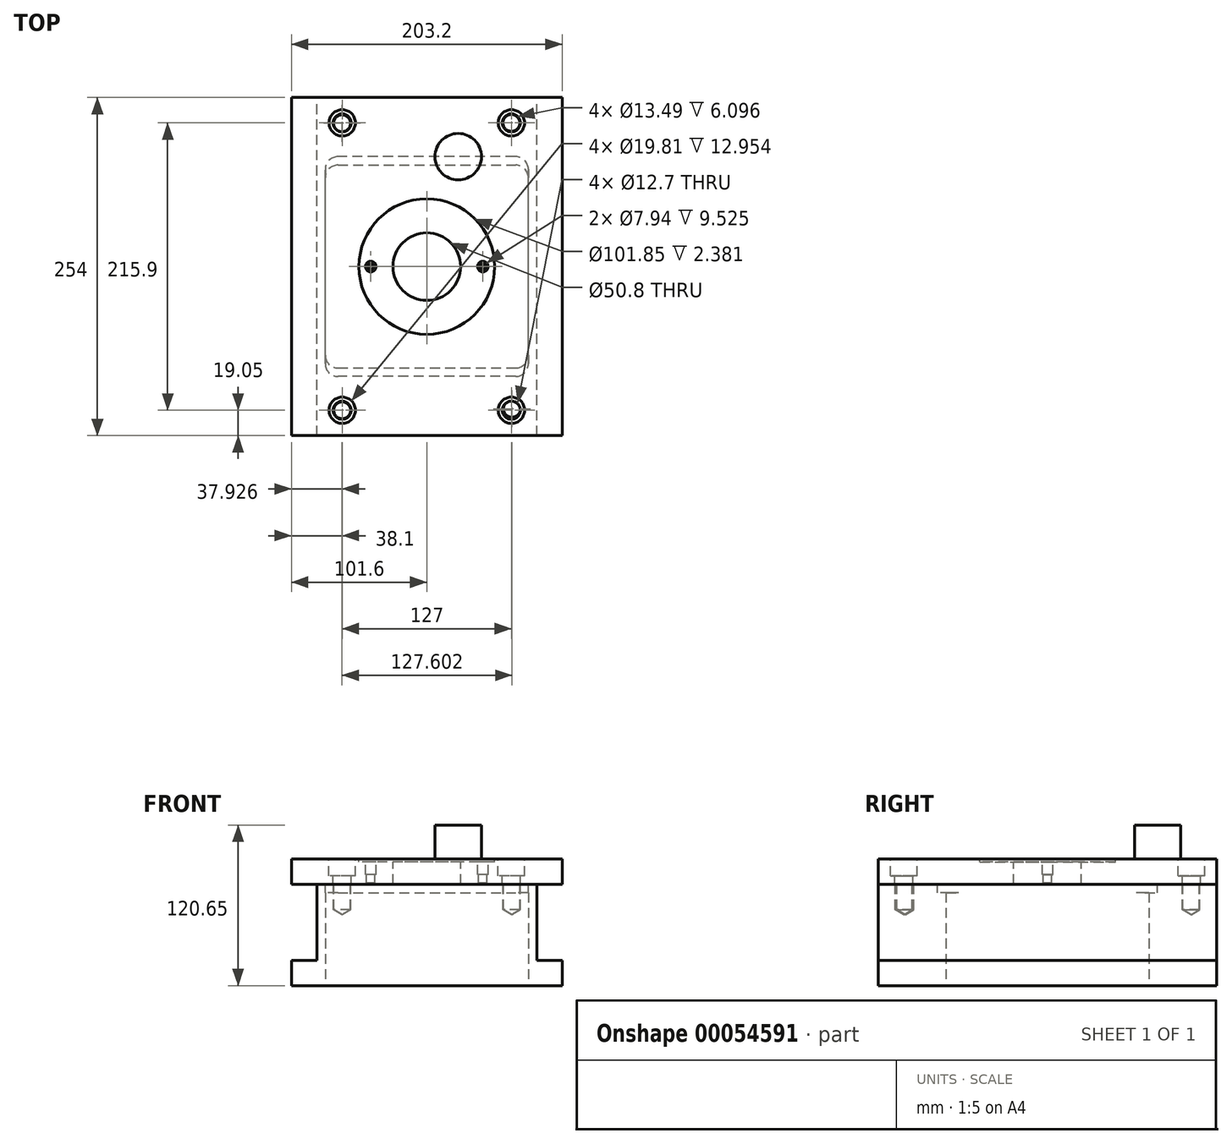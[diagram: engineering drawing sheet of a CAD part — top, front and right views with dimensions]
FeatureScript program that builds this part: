
annotation { "Feature Type Name" : "Feature", "Feature Type Description" : "" }
export const myFeature = defineFeature(function(context is Context, id is Id, definition is map)
    precondition{}
    {
        {
            var Q0;
            Q0=qCreatedBy(makeId("Front.planeOp"),FACE);
            var sketch = newSketch(context, id + "F0", { "sketchPlane" : qUnion([Q0])});
            skLineSegment(sketch, "E0", {"start": v(-101.6, 0) * mm, "end": v(101.6, 0) * mm});
            skLineSegment(sketch, "E1", {"start": v(101.6, 0) * mm, "end": v(101.6, 19.05) * mm});
            skLineSegment(sketch, "E2", {"start": v(101.6, 19.05) * mm, "end": v(82.55, 19.05) * mm});
            skLineSegment(sketch, "E3", {"start": v(82.55, 19.05) * mm, "end": v(82.55, 76.2) * mm});
            skLineSegment(sketch, "E4", {"start": v(82.55, 76.2) * mm, "end": v(-82.55, 76.2) * mm});
            skLineSegment(sketch, "E5", {"start": v(-82.55, 76.2) * mm, "end": v(-82.55, 19.05) * mm});
            skLineSegment(sketch, "E6", {"start": v(-82.55, 19.05) * mm, "end": v(-101.6, 19.05) * mm});
            skLineSegment(sketch, "E7", {"start": v(-101.6, 19.05) * mm, "end": v(-101.6, 0) * mm});
            skSolve(sketch);
        }
        {
            var Q0;
            Q0 = qSketchRegion(id + "F0", true);
            extrude(context, id + "F1", {"entities" : qUnion([Q0]), "endBound" : BoundingType.SYMMETRIC, "depth" : 254 * mm});
        }
        {
            var Q0;
            Q0=makeQuery(id+"F1.opExtrude","SWEPT_FACE",FACE,{"disambiguationData":[OSD([sQuery(id+"F0.wireOp",EDGE,"E0")])]});
            var sketch = newSketch(context, id + "F2", { "sketchPlane" : qUnion([Q0])});
            skLineSegment(sketch, "E8.bottom", {"start": v(-66.67, 76.2) * mm, "end": v(66.67, 76.2) * mm});
            skLineSegment(sketch, "E8.top", {"start": v(-66.67, -76.2) * mm, "end": v(66.67, -76.2) * mm});
            skLineSegment(sketch, "E8.left", {"start": v(-76.2, 66.67) * mm, "end": v(-76.2, -66.68) * mm});
            skLineSegment(sketch, "E8.right", {"start": v(76.2, 66.68) * mm, "end": v(76.2, -66.67) * mm});
            skPoint(sketch, "E9.visualSharp", {"position": v(-76.2, 76.2) * mm});
            skArc(sketch, "E9.filletArc", {"start": v(-66.67, 76.2) * mm, "mid": v(-73.41, 73.41) * mm, "end": v(-76.2, 66.67) * mm});
            skPoint(sketch, "E10.visualSharp", {"position": v(-76.2, -76.2) * mm});
            skArc(sketch, "E10.filletArc", {"start": v(-76.2, -66.68) * mm, "mid": v(-73.41, -73.41) * mm, "end": v(-66.67, -76.2) * mm});
            skPoint(sketch, "E11.visualSharp", {"position": v(76.2, -76.2) * mm});
            skArc(sketch, "E11.filletArc", {"start": v(66.67, -76.2) * mm, "mid": v(73.41, -73.41) * mm, "end": v(76.2, -66.67) * mm});
            skPoint(sketch, "E12.visualSharp", {"position": v(76.2, 76.2) * mm});
            skArc(sketch, "E12.filletArc", {"start": v(76.2, 66.68) * mm, "mid": v(73.41, 73.41) * mm, "end": v(66.67, 76.2) * mm});
            skSolve(sketch);
        }
        {
            var Q0;
            Q0 = qSketchRegion(id + "F2", true);
            extrude(context, id + "F3", {"entities" : qUnion([Q0]), "operationType" : NewBodyOperationType.REMOVE, "oppositeDirection" : true, "depth" : 76.2 * mm});
        }
        {
            var Q0;
            Q0=makeQuery(id+"F1.opExtrude","SWEPT_FACE",FACE,{"disambiguationData":[OSD([sQuery(id+"F0.wireOp",EDGE,"E4")])]});
            var sketch = newSketch(context, id + "F4", { "sketchPlane" : qUnion([Q0])});
            skLineSegment(sketch, "E13.bottom", {"start": v(66.67, 82.55) * mm, "end": v(-66.68, 82.55) * mm});
            skLineSegment(sketch, "E13.top", {"start": v(66.67, -82.55) * mm, "end": v(-66.67, -82.55) * mm});
            skLineSegment(sketch, "E13.left", {"start": v(76.2, 73.03) * mm, "end": v(76.2, -73.03) * mm});
            skLineSegment(sketch, "E13.right", {"start": v(-76.2, 73.03) * mm, "end": v(-76.2, -73.02) * mm});
            skPoint(sketch, "E14.visualSharp", {"position": v(-76.2, 82.55) * mm});
            skArc(sketch, "E14.filletArc", {"start": v(-66.68, 82.55) * mm, "mid": v(-73.41, 79.76) * mm, "end": v(-76.2, 73.03) * mm});
            skPoint(sketch, "E15.visualSharp", {"position": v(-76.2, -82.55) * mm});
            skArc(sketch, "E15.filletArc", {"start": v(-76.2, -73.02) * mm, "mid": v(-73.41, -79.76) * mm, "end": v(-66.67, -82.55) * mm});
            skPoint(sketch, "E16.visualSharp", {"position": v(76.2, -82.55) * mm});
            skArc(sketch, "E16.filletArc", {"start": v(66.67, -82.55) * mm, "mid": v(73.41, -79.76) * mm, "end": v(76.2, -73.03) * mm});
            skPoint(sketch, "E17.visualSharp", {"position": v(76.2, 82.55) * mm});
            skArc(sketch, "E17.filletArc", {"start": v(76.2, 73.03) * mm, "mid": v(73.41, 79.76) * mm, "end": v(66.67, 82.55) * mm});
            skSolve(sketch);
        }
        {
            var Q0;
            Q0 = qSketchRegion(id + "F4", true);
            extrude(context, id + "F5", {"entities" : qUnion([Q0]), "operationType" : NewBodyOperationType.REMOVE, "oppositeDirection" : true, "depth" : 6.35 * mm});
        }
        {
            var Q0;
            Q0=makeQuery(id+"F1.opExtrude","SWEPT_FACE",FACE,{"disambiguationData":[OSD([sQuery(id+"F0.wireOp",EDGE,"E4")])]});
            var sketch = newSketch(context, id + "F15", { "sketchPlane" : qUnion([Q0])});
            skSolve(sketch);
        }
        {
            var Q0;
            {var subQ0=sQuery(id+"F0.wireOp",EDGE,"E4");Q0=makeQuery(id+"F15.imprint","IMPRINT",FACE,{"disambiguationData":[TD([[makeQuery(id+"F15.imprint","IMPRINT",EDGE,{"derivedFrom":makeQuery(id+"F1.opExtrude","CAP_EDGE",EDGE,{"disambiguationData":[OSD([subQ0])],"isStart":true})}),1.0]])]});}
            var sketch = newSketch(context, id + "F6", { "sketchPlane" : qUnion([Q0])});
            skLineSegment(sketch, "E18.bottom", {"start": v(101.6, -127) * mm, "end": v(-101.6, -127) * mm});
            skLineSegment(sketch, "E18.top", {"start": v(101.6, 127) * mm, "end": v(-101.6, 127) * mm});
            skLineSegment(sketch, "E18.left", {"start": v(101.6, -127) * mm, "end": v(101.6, 127) * mm});
            skLineSegment(sketch, "E18.right", {"start": v(-101.6, -127) * mm, "end": v(-101.6, 127) * mm});
            skSolve(sketch);
        }
        {
            var Q0;
            Q0 = qSketchRegion(id + "F6", true);
            extrude(context, id + "F16", {"entities" : qUnion([Q0]), "depth" : 19.05 * mm});
        }
        {
            var Q0;
            Q0=makeQuery(id+"F16.opExtrude","CAP_FACE",FACE,{"disambiguationData":[OSD([sQuery(id+"F6.wireOp",EDGE,"E18.bottom"),sQuery(id+"F6.wireOp",EDGE,"E18.top"),sQuery(id+"F6.wireOp",EDGE,"E18.left"),sQuery(id+"F6.wireOp",EDGE,"E18.right")])],"isStart":false});
            var sketch = newSketch(context, id + "F17", { "sketchPlane" : qUnion([Q0])});
            skCircle(sketch, "E19", {"center": v(0, 0) * mm, "radius": 50.93 * mm});
            skSolve(sketch);
        }
        {
            var Q0;
            Q0 = qSketchRegion(id + "F17", true);
            extrude(context, id + "F7", {"entities" : qUnion([Q0]), "operationType" : NewBodyOperationType.REMOVE, "oppositeDirection" : true, "depth" : 2.38 * mm});
        }
        {
            var Q0;
            Q0=makeQuery(id+"F7.boolean.opBoolean","COPY",FACE,{"derivedFrom":makeQuery(id+"F7.opExtrude","CAP_FACE",FACE,{"disambiguationData":[OSD([sQuery(id+"F17.wireOp",EDGE,"E19")])],"isStart":false})});
            var sketch = newSketch(context, id + "F8", { "sketchPlane" : qUnion([Q0])});
            skCircle(sketch, "E20", {"center": v(0, 0) * mm, "radius": 25.4 * mm});
            skSolve(sketch);
        }
        {
            var Q0;
            Q0 = qSketchRegion(id + "F8", true);
            extrude(context, id + "F18", {"entities" : qUnion([Q0]), "operationType" : NewBodyOperationType.REMOVE, "oppositeDirection" : true, "depth" : 25.4 * mm});
        }
        {
            var Q0;
            Q0=makeQuery(id+"F7.boolean.opBoolean","COPY",FACE,{"derivedFrom":makeQuery(id+"F7.opExtrude","CAP_FACE",FACE,{"disambiguationData":[OSD([sQuery(id+"F17.wireOp",EDGE,"E19")])],"isStart":false})});
            var sketch = newSketch(context, id + "F9", { "sketchPlane" : qUnion([Q0])});
            skPoint(sketch, "E21", {"position": v(42.07, 0) * mm});
            skPoint(sketch, "E22", {"position": v(-42.07, 0) * mm});
            skSolve(sketch);
        }
        {
            var Q0;
            Q0=sQuery(id+"F9.wireOp",VERTEX,"E21");
            var Q1;
            Q1=sQuery(id+"F9.wireOp",VERTEX,"E22");
            var Q2;
            Q2=makeQuery(id+"F16.opExtrude","SWEPT_BODY",BODY,{"disambiguationData":[OSD([sQuery(id+"F6.wireOp",EDGE,"E18.bottom"),sQuery(id+"F6.wireOp",EDGE,"E18.top"),sQuery(id+"F6.wireOp",EDGE,"E18.left"),sQuery(id+"F6.wireOp",EDGE,"E18.right")])]});
            hole(context, id + "F19", {"style" : HoleStyle.C_BORE, "holeDiameter" : 6.35 * mm, "cBoreDiameter" : 7.94 * mm, "cBoreDepth" : 9.52 * mm, "endStyle" : HoleEndStyle.BLIND, "holeDepth" : 15.88 * mm, "locations" : qUnion([Q0, Q1]), "scope" : qUnion([Q2])});
        }
        {
            var Q0;
            Q0=makeQuery(id+"F16.opExtrude","CAP_FACE",FACE,{"disambiguationData":[OSD([sQuery(id+"F6.wireOp",EDGE,"E18.bottom"),sQuery(id+"F6.wireOp",EDGE,"E18.top"),sQuery(id+"F6.wireOp",EDGE,"E18.left"),sQuery(id+"F6.wireOp",EDGE,"E18.right")])],"isStart":false});
            var sketch = newSketch(context, id + "F10", { "sketchPlane" : qUnion([Q0])});
            skLineSegment(sketch, "E23.bottom", {"start": v(-63.5, 107.95) * mm, "end": v(63.5, 107.95) * mm});
            skLineSegment(sketch, "E23.top", {"start": v(-63.5, -107.95) * mm, "end": v(63.5, -107.95) * mm});
            skLineSegment(sketch, "E23.left", {"start": v(-63.5, 107.95) * mm, "end": v(-63.5, -107.95) * mm});
            skLineSegment(sketch, "E23.right", {"start": v(63.5, 107.95) * mm, "end": v(63.5, -107.95) * mm});
            skLineSegment(sketch, "E24", {"start": v(63.5, 107.95) * mm, "end": v(-63.5, -107.95) * mm});
            skPoint(sketch, "E25", {"position": v(-63.5, 107.95) * mm});
            skPoint(sketch, "E26", {"position": v(63.5, 107.95) * mm});
            skPoint(sketch, "E27", {"position": v(63.5, -107.95) * mm});
            skPoint(sketch, "E28", {"position": v(-63.5, -107.95) * mm});
            skSolve(sketch);
        }
        {
            var Q0;
            Q0=sQuery(id+"F10.wireOp",VERTEX,"E25");
            var Q1;
            Q1=sQuery(id+"F10.wireOp",VERTEX,"E26");
            var Q2;
            Q2=sQuery(id+"F10.wireOp",VERTEX,"E27");
            var Q3;
            Q3=sQuery(id+"F10.wireOp",VERTEX,"E28");
            var Q4;
            Q4=makeQuery(id+"F16.opExtrude","SWEPT_BODY",BODY,{"disambiguationData":[OSD([sQuery(id+"F6.wireOp",EDGE,"E18.bottom"),sQuery(id+"F6.wireOp",EDGE,"E18.top"),sQuery(id+"F6.wireOp",EDGE,"E18.left"),sQuery(id+"F6.wireOp",EDGE,"E18.right")])]});
            hole(context, id + "F11", {"style" : HoleStyle.C_BORE, "holeDiameter" : 13.5 * mm, "cBoreDiameter" : 19.8 * mm, "cBoreDepth" : 12.95 * mm, "endStyle" : HoleEndStyle.THROUGH, "locations" : qUnion([Q0, Q1, Q2, Q3]), "scope" : qUnion([Q4])});
        }
        {
            var Q0;
            {var subQ0=sQuery(id+"F0.wireOp",EDGE,"E4");Q0=makeQuery(id+"F15.imprint","IMPRINT",FACE,{"disambiguationData":[TD([[makeQuery(id+"F15.imprint","IMPRINT",EDGE,{"derivedFrom":makeQuery(id+"F1.opExtrude","CAP_EDGE",EDGE,{"disambiguationData":[OSD([subQ0])],"isStart":true})}),1.0]])]});}
            var sketch = newSketch(context, id + "F12", { "sketchPlane" : qUnion([Q0])});
            skPoint(sketch, "E29", {"position": v(-63.67, 107.64) * mm});
            skPoint(sketch, "E30", {"position": v(63.5, 107.95) * mm});
            skPoint(sketch, "E31", {"position": v(63.93, -106.82) * mm});
            skPoint(sketch, "E32", {"position": v(-63.5, -107.95) * mm});
            skSolve(sketch);
        }
        {
            var Q0;
            Q0=sQuery(id+"F12.wireOp",VERTEX,"E29");
            var Q1;
            Q1=sQuery(id+"F12.wireOp",VERTEX,"E30");
            var Q2;
            Q2=sQuery(id+"F12.wireOp",VERTEX,"E31");
            var Q3;
            Q3=sQuery(id+"F12.wireOp",VERTEX,"E32");
            var Q4;
            Q4=makeQuery(id+"F1.opExtrude","SWEPT_BODY",BODY,{"disambiguationData":[OSD([sQuery(id+"F0.wireOp",EDGE,"E0"),sQuery(id+"F0.wireOp",EDGE,"E1"),sQuery(id+"F0.wireOp",EDGE,"E2"),sQuery(id+"F0.wireOp",EDGE,"E3"),sQuery(id+"F0.wireOp",EDGE,"E4"),sQuery(id+"F0.wireOp",EDGE,"E5"),sQuery(id+"F0.wireOp",EDGE,"E6"),sQuery(id+"F0.wireOp",EDGE,"E7")])]});
            hole(context, id + "F13", {"style" : HoleStyle.SIMPLE, "holeDiameter" : 12.7 * mm, "endStyle" : HoleEndStyle.BLIND, "holeDepth" : 19.05 * mm, "locations" : qUnion([Q0, Q1, Q2, Q3]), "scope" : qUnion([Q4])});
        }
        {
            var Q0;
            Q0=makeQuery(id+"F16.opExtrude","CAP_FACE",FACE,{"disambiguationData":[OSD([sQuery(id+"F6.wireOp",EDGE,"E18.bottom"),sQuery(id+"F6.wireOp",EDGE,"E18.top"),sQuery(id+"F6.wireOp",EDGE,"E18.left"),sQuery(id+"F6.wireOp",EDGE,"E18.right")])],"isStart":false});
            var sketch = newSketch(context, id + "F20", { "sketchPlane" : qUnion([Q0])});
            skCircle(sketch, "E33", {"center": v(23.59, 82.6) * mm, "radius": 17.44 * mm});
            skSolve(sketch);
        }
        {
            var Q0;
            Q0 = qSketchRegion(id + "F20", true);
            extrude(context, id + "F14", {"entities" : qUnion([Q0]), "operationType" : NewBodyOperationType.ADD, "depth" : 25.4 * mm});
        }
    });
